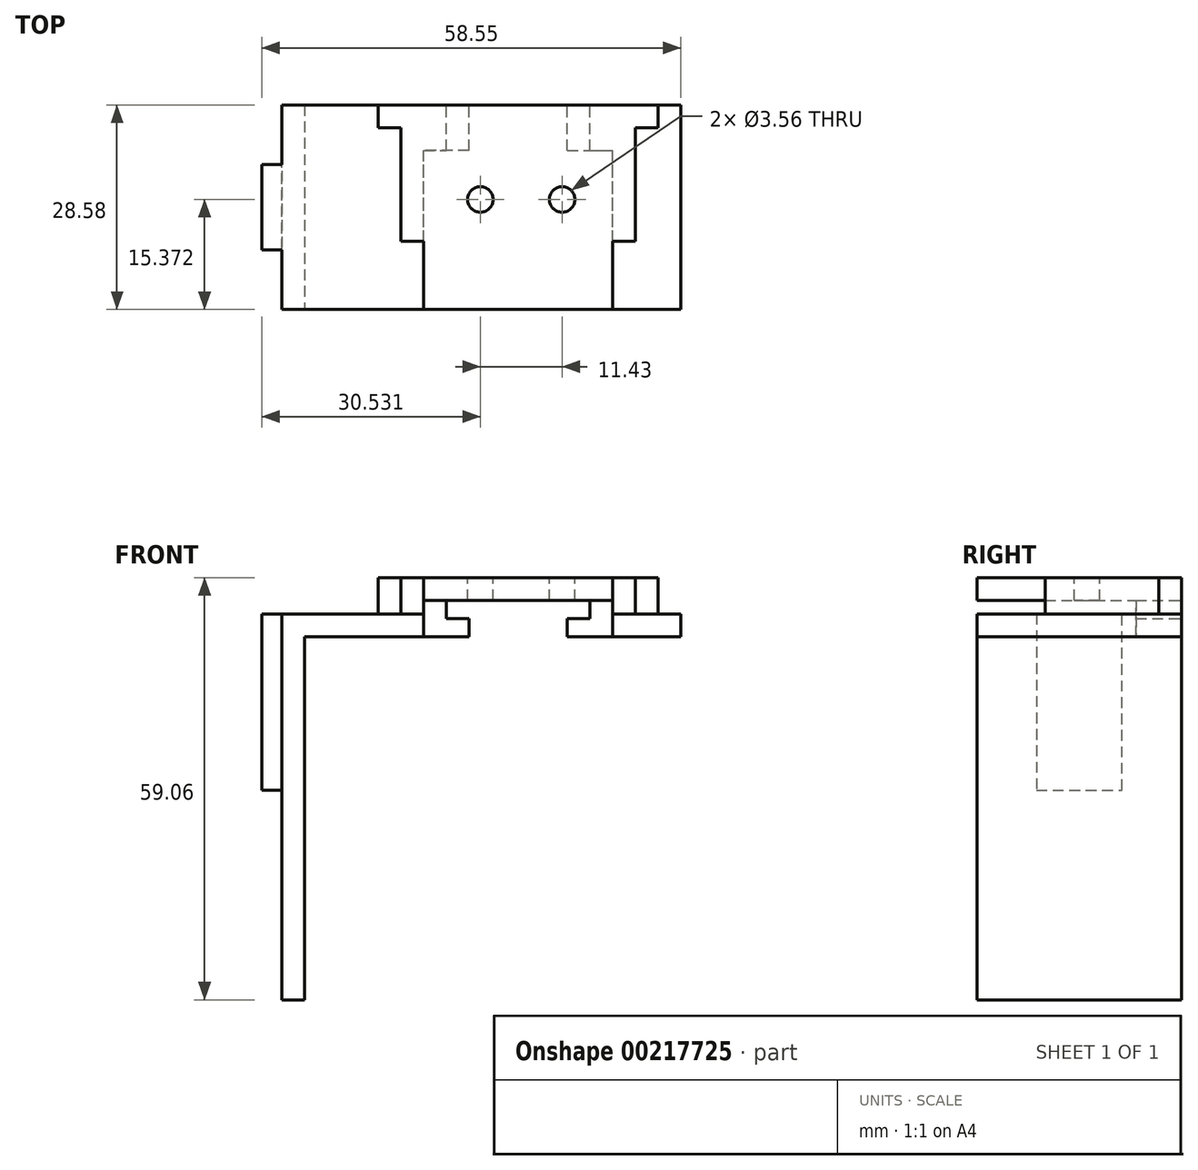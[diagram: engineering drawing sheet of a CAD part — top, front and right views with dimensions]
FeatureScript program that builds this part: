
annotation { "Feature Type Name" : "Feature", "Feature Type Description" : "" }
export const myFeature = defineFeature(function(context is Context, id is Id, definition is map)
    precondition{}
    {
        {
            var Q0;
            Q0=qCreatedBy(makeId("Front.planeOp"),FACE);
            var sketch = newSketch(context, id + "F0", { "sketchPlane" : qUnion([Q0])});
            skLineSegment(sketch, "E0", {"start": v(0, 0) * mm, "end": v(3.18, 0) * mm});
            skLineSegment(sketch, "E1", {"start": v(0, 0) * mm, "end": v(0, 2.54) * mm});
            skLineSegment(sketch, "E2", {"start": v(0, 2.54) * mm, "end": v(3.18, 2.54) * mm});
            skLineSegment(sketch, "E3", {"start": v(3.18, 0) * mm, "end": v(6.35, 0) * mm});
            skLineSegment(sketch, "E4", {"start": v(6.35, 0) * mm, "end": v(6.35, 5.08) * mm});
            skLineSegment(sketch, "E5.MirrorCS", {"start": v(-20.07, 0) * mm, "end": v(-20.07, 5.08) * mm});
            skLineSegment(sketch, "E6.MirrorCS", {"start": v(-16.9, 0) * mm, "end": v(-20.07, 0) * mm});
            skLineSegment(sketch, "E7.MirrorCS", {"start": v(-13.72, 0) * mm, "end": v(-13.72, 2.54) * mm});
            skLineSegment(sketch, "E8.MirrorCS", {"start": v(-13.72, 2.54) * mm, "end": v(-16.9, 2.54) * mm});
            skLineSegment(sketch, "E9.MirrorCS", {"start": v(-13.72, 0) * mm, "end": v(-16.9, 0) * mm});
            skLineSegment(sketch, "E10", {"start": v(-16.9, 2.54) * mm, "end": v(-16.9, 5.08) * mm});
            skLineSegment(sketch, "E11", {"start": v(-16.9, 5.08) * mm, "end": v(3.18, 5.08) * mm});
            skLineSegment(sketch, "E12", {"start": v(3.18, 5.08) * mm, "end": v(3.18, 2.54) * mm});
            skLineSegment(sketch, "E13", {"start": v(6.35, 5.08) * mm, "end": v(6.35, 8.26) * mm});
            skLineSegment(sketch, "E14", {"start": v(6.35, 8.26) * mm, "end": v(-20.07, 8.26) * mm});
            skLineSegment(sketch, "E15", {"start": v(-20.07, 8.26) * mm, "end": v(-20.07, 5.08) * mm});
            skSolve(sketch);
        }
        {
            var Q0;
            Q0 = qSketchRegion(id + "F0", true);
            extrude(context, id + "F1", {"entities" : qUnion([Q0]), "depth" : 6.35 * mm});
        }
        {
            var Q0;
            Q0=makeQuery(id+"F1.opExtrude","CAP_FACE",FACE,{"disambiguationData":[OSD([sQuery(id+"F0.wireOp",EDGE,"E0"),sQuery(id+"F0.wireOp",EDGE,"E1"),sQuery(id+"F0.wireOp",EDGE,"E2"),sQuery(id+"F0.wireOp",EDGE,"E3"),sQuery(id+"F0.wireOp",EDGE,"E4"),sQuery(id+"F0.wireOp",EDGE,"E5.MirrorCS"),sQuery(id+"F0.wireOp",EDGE,"E6.MirrorCS"),sQuery(id+"F0.wireOp",EDGE,"E7.MirrorCS"),sQuery(id+"F0.wireOp",EDGE,"E8.MirrorCS"),sQuery(id+"F0.wireOp",EDGE,"E9.MirrorCS"),sQuery(id+"F0.wireOp",EDGE,"E10"),sQuery(id+"F0.wireOp",EDGE,"E11"),sQuery(id+"F0.wireOp",EDGE,"E12"),sQuery(id+"F0.wireOp",EDGE,"E13"),sQuery(id+"F0.wireOp",EDGE,"E14"),sQuery(id+"F0.wireOp",EDGE,"E15")])],"isStart":false});
            var sketch = newSketch(context, id + "F2", { "sketchPlane" : qUnion([Q0])});
            skLineSegment(sketch, "E16.bottom", {"start": v(-20.07, 8.26) * mm, "end": v(6.35, 8.26) * mm});
            skLineSegment(sketch, "E16.top", {"start": v(-20.07, 5.08) * mm, "end": v(6.35, 5.08) * mm});
            skLineSegment(sketch, "E16.left", {"start": v(-20.07, 8.26) * mm, "end": v(-20.07, 5.08) * mm});
            skLineSegment(sketch, "E16.right", {"start": v(6.35, 8.26) * mm, "end": v(6.35, 5.08) * mm});
            skSolve(sketch);
        }
        {
            var Q0;
            Q0 = qSketchRegion(id + "F2", true);
            extrude(context, id + "F3", {"entities" : qUnion([Q0]), "operationType" : NewBodyOperationType.ADD, "depth" : 22.22 * mm});
        }
        {
            var Q0;
            Q0=makeQuery(id+"F3.boolean.opBoolean","MERGE",FACE,{"derivedFrom":[makeQuery(id+"F1.opExtrude","SWEPT_FACE",FACE,{"disambiguationData":[OSD([sQuery(id+"F0.wireOp",EDGE,"E14")])]}),makeQuery(id+"F3.opExtrude","SWEPT_FACE",FACE,{"disambiguationData":[OSD([sQuery(id+"F2.wireOp",EDGE,"E16.bottom")])]})]});
            var sketch = newSketch(context, id + "F4", { "sketchPlane" : qUnion([Q0])});
            skLineSegment(sketch, "E17.bottom", {"start": v(-20.07, 0) * mm, "end": v(-23.24, 0) * mm});
            skLineSegment(sketch, "E17.top", {"start": v(-20.07, -19.05) * mm, "end": v(-23.24, -19.05) * mm});
            skLineSegment(sketch, "E17.left", {"start": v(-20.07, 0) * mm, "end": v(-20.07, -19.05) * mm});
            skLineSegment(sketch, "E17.right", {"start": v(-23.24, 0) * mm, "end": v(-23.24, -19.05) * mm});
            skLineSegment(sketch, "E18.bottom", {"start": v(6.35, 0) * mm, "end": v(9.53, 0) * mm});
            skLineSegment(sketch, "E18.top", {"start": v(6.35, -19.05) * mm, "end": v(9.53, -19.05) * mm});
            skLineSegment(sketch, "E18.left", {"start": v(6.35, 0) * mm, "end": v(6.35, -19.05) * mm});
            skLineSegment(sketch, "E18.right", {"start": v(9.53, 0) * mm, "end": v(9.53, -19.05) * mm});
            skSolve(sketch);
        }
        {
            var Q0;
            Q0 = qSketchRegion(id + "F4", true);
            var Q1;
            Q1=makeQuery(id+"F1.opExtrude","SWEPT_FACE",FACE,{"disambiguationData":[OSD([sQuery(id+"F0.wireOp",EDGE,"E6.MirrorCS"),sQuery(id+"F0.wireOp",EDGE,"E9.MirrorCS")])]});
            extrude(context, id + "F5", {"entities" : qUnion([Q0]), "operationType" : NewBodyOperationType.ADD, "endBound" : BoundingType.UP_TO_SURFACE, "oppositeDirection" : true, "endBoundEntityFace" : qUnion([Q1]), "depth" : 9.52 * mm});
        }
        {
            var Q0;
            Q0=makeQuery(id+"F5.opExtrude","SWEPT_FACE",FACE,{"disambiguationData":[OSD([sQuery(id+"F4.wireOp",EDGE,"E17.top")])]});
            var sketch = newSketch(context, id + "F6", { "sketchPlane" : qUnion([Q0])});
            skLineSegment(sketch, "E19.bottom", {"start": v(-20.07, 0) * mm, "end": v(-23.24, 0) * mm});
            skLineSegment(sketch, "E19.top", {"start": v(-20.07, 3.18) * mm, "end": v(-23.24, 3.18) * mm});
            skLineSegment(sketch, "E19.left", {"start": v(-20.07, 0) * mm, "end": v(-20.07, 3.18) * mm});
            skLineSegment(sketch, "E19.right", {"start": v(-23.24, 0) * mm, "end": v(-23.24, 3.17) * mm});
            skSolve(sketch);
        }
        {
            var Q0;
            Q0 = qSketchRegion(id + "F6", true);
            var Q1;
            Q1=makeQuery(id+"F3.opExtrude","CAP_FACE",FACE,{"disambiguationData":[OSD([sQuery(id+"F2.wireOp",EDGE,"E16.bottom"),sQuery(id+"F2.wireOp",EDGE,"E16.top"),sQuery(id+"F2.wireOp",EDGE,"E16.left"),sQuery(id+"F2.wireOp",EDGE,"E16.right")])],"isStart":false});
            extrude(context, id + "F7", {"entities" : qUnion([Q0]), "operationType" : NewBodyOperationType.ADD, "endBound" : BoundingType.UP_TO_SURFACE, "endBoundEntityFace" : qUnion([Q1]), "depth" : 25.4 * mm});
        }
        {
            var Q0;
            Q0=makeQuery(id+"F5.opExtrude","SWEPT_FACE",FACE,{"disambiguationData":[OSD([sQuery(id+"F4.wireOp",EDGE,"E18.top")])]});
            var sketch = newSketch(context, id + "F8", { "sketchPlane" : qUnion([Q0])});
            skLineSegment(sketch, "E20.bottom", {"start": v(6.35, 0) * mm, "end": v(9.53, 0) * mm});
            skLineSegment(sketch, "E20.top", {"start": v(6.35, 3.18) * mm, "end": v(9.53, 3.18) * mm});
            skLineSegment(sketch, "E20.left", {"start": v(6.35, 0) * mm, "end": v(6.35, 3.18) * mm});
            skLineSegment(sketch, "E20.right", {"start": v(9.53, 0) * mm, "end": v(9.53, 3.18) * mm});
            skSolve(sketch);
        }
        {
            var Q0;
            Q0 = qSketchRegion(id + "F8", true);
            var Q1;
            Q1=makeQuery(id+"F3.opExtrude","CAP_FACE",FACE,{"disambiguationData":[OSD([sQuery(id+"F2.wireOp",EDGE,"E16.bottom"),sQuery(id+"F2.wireOp",EDGE,"E16.top"),sQuery(id+"F2.wireOp",EDGE,"E16.left"),sQuery(id+"F2.wireOp",EDGE,"E16.right")])],"isStart":false});
            extrude(context, id + "F9", {"entities" : qUnion([Q0]), "operationType" : NewBodyOperationType.ADD, "endBound" : BoundingType.UP_TO_SURFACE, "endBoundEntityFace" : qUnion([Q1]), "depth" : 25.4 * mm});
        }
        {
            var Q0;
            Q0=makeQuery(id+"F7.boolean.opBoolean","MERGE",FACE,{"derivedFrom":[makeQuery(id+"F5.opExtrude","SWEPT_FACE",FACE,{"disambiguationData":[OSD([sQuery(id+"F4.wireOp",EDGE,"E17.right")])]}),makeQuery(id+"F7.opExtrude","SWEPT_FACE",FACE,{"disambiguationData":[OSD([sQuery(id+"F6.wireOp",EDGE,"E19.right")])]})]});
            var sketch = newSketch(context, id + "F10", { "sketchPlane" : qUnion([Q0])});
            skLineSegment(sketch, "E21.bottom", {"start": v(28.57, 3.17) * mm, "end": v(0, 3.17) * mm});
            skLineSegment(sketch, "E21.top", {"start": v(28.57, 0) * mm, "end": v(0, 0) * mm});
            skLineSegment(sketch, "E21.left", {"start": v(28.57, 3.17) * mm, "end": v(28.57, 0) * mm});
            skLineSegment(sketch, "E21.right", {"start": v(0, 3.17) * mm, "end": v(0, 0) * mm});
            skSolve(sketch);
        }
        {
            var Q0;
            Q0 = qSketchRegion(id + "F10", true);
            extrude(context, id + "F11", {"entities" : qUnion([Q0]), "operationType" : NewBodyOperationType.ADD, "depth" : 13.46 * mm});
        }
        {
            var Q0;
            {var subQ0=sQuery(id+"F0.wireOp",EDGE,"E9.MirrorCS");var subQ1=sQuery(id+"F0.wireOp",EDGE,"E6.MirrorCS");Q0=makeQuery(id+"F11.boolean.opBoolean","MERGE",FACE,{"derivedFrom":[makeQuery(id+"F7.boolean.opBoolean","MERGE",FACE,{"derivedFrom":[makeQuery(id+"F5.boolean.opBoolean","MERGE",FACE,{"derivedFrom":[makeQuery(id+"F1.opExtrude","SWEPT_FACE",FACE,{"disambiguationData":[OSD([subQ1,subQ0])]}),makeQuery(id+"F5.opExtrude","CAP_FACE",FACE,{"disambiguationData":[OSD([subQ1,subQ0]),ownerDisambiguation([makeQuery(id+"F4.imprint","IMPRINT",EDGE,{"derivedFrom":sQuery(id+"F4.wireOp",EDGE,"E17.bottom")})])],"isStart":false})]}),makeQuery(id+"F7.opExtrude","SWEPT_FACE",FACE,{"disambiguationData":[OSD([sQuery(id+"F6.wireOp",EDGE,"E19.bottom")])]})]}),makeQuery(id+"F11.opExtrude","SWEPT_FACE",FACE,{"disambiguationData":[OSD([sQuery(id+"F10.wireOp",EDGE,"E21.top")])]})]});}
            var sketch = newSketch(context, id + "F12", { "sketchPlane" : qUnion([Q0])});
            skLineSegment(sketch, "E22.bottom", {"start": v(-36.7, 0) * mm, "end": v(-39.88, 0) * mm});
            skLineSegment(sketch, "E22.top", {"start": v(-36.7, 28.58) * mm, "end": v(-39.88, 28.58) * mm});
            skLineSegment(sketch, "E22.left", {"start": v(-36.7, 0) * mm, "end": v(-36.7, 28.58) * mm});
            skLineSegment(sketch, "E22.right", {"start": v(-39.88, 0) * mm, "end": v(-39.88, 28.58) * mm});
            skSolve(sketch);
        }
        {
            var Q0;
            Q0 = qSketchRegion(id + "F12", true);
            extrude(context, id + "F13", {"entities" : qUnion([Q0]), "operationType" : NewBodyOperationType.ADD, "depth" : 50.8 * mm, "hasSecondDirection" : true, "secondDirectionOppositeDirection" : true, "secondDirectionDepth" : 3.17 * mm});
        }
        {
            var Q0;
            Q0=makeQuery(id+"F13.opExtrude","SWEPT_FACE",FACE,{"disambiguationData":[OSD([sQuery(id+"F12.wireOp",EDGE,"E22.right")])]});
            var sketch = newSketch(context, id + "F14", { "sketchPlane" : qUnion([Q0])});
            skLineSegment(sketch, "E23", {"start": v(14.29, 3.18) * mm, "end": v(20.26, 3.18) * mm});
            skLineSegment(sketch, "E24", {"start": v(20.26, 3.18) * mm, "end": v(20.26, -21.46) * mm});
            skLineSegment(sketch, "E25", {"start": v(20.26, -21.46) * mm, "end": v(8.32, -21.46) * mm});
            skLineSegment(sketch, "E26", {"start": v(8.32, -21.46) * mm, "end": v(8.32, 3.17) * mm});
            skLineSegment(sketch, "E27", {"start": v(8.32, 3.18) * mm, "end": v(14.29, 3.18) * mm});
            skSolve(sketch);
        }
        {
            var Q0;
            Q0 = qSketchRegion(id + "F14", true);
            extrude(context, id + "F15", {"entities" : qUnion([Q0]), "operationType" : NewBodyOperationType.ADD, "depth" : 2.8 * mm});
        }
        {
            var Q0;
            Q0=makeQuery(id+"F5.boolean.opBoolean","MERGE",FACE,{"derivedFrom":[makeQuery(id+"F3.boolean.opBoolean","MERGE",FACE,{"derivedFrom":[makeQuery(id+"F1.opExtrude","SWEPT_FACE",FACE,{"disambiguationData":[OSD([sQuery(id+"F0.wireOp",EDGE,"E14")])]}),makeQuery(id+"F3.opExtrude","SWEPT_FACE",FACE,{"disambiguationData":[OSD([sQuery(id+"F2.wireOp",EDGE,"E16.bottom")])]})]}),makeQuery(id+"F5.opExtrude","CAP_FACE",FACE,{"disambiguationData":[OSD([sQuery(id+"F4.wireOp",EDGE,"E17.bottom"),sQuery(id+"F4.wireOp",EDGE,"E17.top"),sQuery(id+"F4.wireOp",EDGE,"E17.left"),sQuery(id+"F4.wireOp",EDGE,"E17.right")])],"isStart":true}),makeQuery(id+"F5.opExtrude","CAP_FACE",FACE,{"disambiguationData":[OSD([sQuery(id+"F4.wireOp",EDGE,"E18.bottom"),sQuery(id+"F4.wireOp",EDGE,"E18.top"),sQuery(id+"F4.wireOp",EDGE,"E18.left"),sQuery(id+"F4.wireOp",EDGE,"E18.right")])],"isStart":true})]});
            var sketch = newSketch(context, id + "F16", { "sketchPlane" : qUnion([Q0])});
            skLineSegment(sketch, "E28", {"start": v(-12.14, 0) * mm, "end": v(-12.14, -13.2) * mm});
            skCircle(sketch, "E29", {"center": v(-12.14, -13.2) * mm, "radius": 1.78 * mm});
            skLineSegment(sketch, "E30", {"start": v(-16.71, 0) * mm, "end": v(-12.14, 0) * mm});
            skLineSegment(sketch, "E31", {"start": v(-12.14, -13.2) * mm, "end": v(-0.7, -13.2) * mm});
            skCircle(sketch, "E32", {"center": v(-0.7, -13.2) * mm, "radius": 1.78 * mm});
            skSolve(sketch);
        }
        {
            var Q0;
            Q0 = qSketchRegion(id + "F16", true);
            extrude(context, id + "F17", {"entities" : qUnion([Q0]), "operationType" : NewBodyOperationType.REMOVE, "oppositeDirection" : true, "depth" : 25.4 * mm});
        }
        {
            var Q0;
            Q0=makeQuery(id+"F15.boolean.opBoolean","MERGE",FACE,{"derivedFrom":[makeQuery(id+"F13.boolean.opBoolean","MERGE",FACE,{"derivedFrom":[makeQuery(id+"F11.boolean.opBoolean","MERGE",FACE,{"derivedFrom":[makeQuery(id+"F7.opExtrude","SWEPT_FACE",FACE,{"disambiguationData":[OSD([sQuery(id+"F6.wireOp",EDGE,"E19.top")])]}),makeQuery(id+"F11.opExtrude","SWEPT_FACE",FACE,{"disambiguationData":[OSD([sQuery(id+"F10.wireOp",EDGE,"E21.bottom")])]})]}),makeQuery(id+"F13.opExtrude","CAP_FACE",FACE,{"disambiguationData":[OSD([sQuery(id+"F12.wireOp",EDGE,"E22.bottom"),sQuery(id+"F12.wireOp",EDGE,"E22.top"),sQuery(id+"F12.wireOp",EDGE,"E22.left"),sQuery(id+"F12.wireOp",EDGE,"E22.right")])],"isStart":true})]}),makeQuery(id+"F15.opExtrude","SWEPT_FACE",FACE,{"disambiguationData":[OSD([sQuery(id+"F14.wireOp",EDGE,"E23"),sQuery(id+"F14.wireOp",EDGE,"E27")])]})]});
            var sketch = newSketch(context, id + "F18", { "sketchPlane" : qUnion([Q0])});
            skLineSegment(sketch, "E33.bottom", {"start": v(-23.24, 0) * mm, "end": v(-26.42, 0) * mm});
            skLineSegment(sketch, "E33.top", {"start": v(-23.24, -3.17) * mm, "end": v(-26.42, -3.18) * mm});
            skLineSegment(sketch, "E33.left", {"start": v(-23.24, 0) * mm, "end": v(-23.24, -3.17) * mm});
            skLineSegment(sketch, "E33.right", {"start": v(-26.42, 0) * mm, "end": v(-26.42, -3.18) * mm});
            skSolve(sketch);
        }
        {
            var Q0;
            Q0 = qSketchRegion(id + "F18", true);
            var Q1;
            Q1=makeQuery(id+"F5.boolean.opBoolean","MERGE",FACE,{"derivedFrom":[makeQuery(id+"F3.boolean.opBoolean","MERGE",FACE,{"derivedFrom":[makeQuery(id+"F1.opExtrude","SWEPT_FACE",FACE,{"disambiguationData":[OSD([sQuery(id+"F0.wireOp",EDGE,"E14")])]}),makeQuery(id+"F3.opExtrude","SWEPT_FACE",FACE,{"disambiguationData":[OSD([sQuery(id+"F2.wireOp",EDGE,"E16.bottom")])]})]}),makeQuery(id+"F5.opExtrude","CAP_FACE",FACE,{"disambiguationData":[OSD([sQuery(id+"F4.wireOp",EDGE,"E17.bottom"),sQuery(id+"F4.wireOp",EDGE,"E17.top"),sQuery(id+"F4.wireOp",EDGE,"E17.left"),sQuery(id+"F4.wireOp",EDGE,"E17.right")])],"isStart":true}),makeQuery(id+"F5.opExtrude","CAP_FACE",FACE,{"disambiguationData":[OSD([sQuery(id+"F4.wireOp",EDGE,"E18.bottom"),sQuery(id+"F4.wireOp",EDGE,"E18.top"),sQuery(id+"F4.wireOp",EDGE,"E18.left"),sQuery(id+"F4.wireOp",EDGE,"E18.right")])],"isStart":true})]});
            extrude(context, id + "F19", {"entities" : qUnion([Q0]), "operationType" : NewBodyOperationType.ADD, "endBound" : BoundingType.UP_TO_SURFACE, "endBoundEntityFace" : qUnion([Q1]), "depth" : 25.4 * mm});
        }
        {
            var Q0;
            Q0=makeQuery(id+"F9.boolean.opBoolean","MERGE",FACE,{"derivedFrom":[makeQuery(id+"F5.opExtrude","SWEPT_FACE",FACE,{"disambiguationData":[OSD([sQuery(id+"F4.wireOp",EDGE,"E18.right")])]}),makeQuery(id+"F9.opExtrude","SWEPT_FACE",FACE,{"disambiguationData":[OSD([sQuery(id+"F8.wireOp",EDGE,"E20.right")])]})]});
            var sketch = newSketch(context, id + "F20", { "sketchPlane" : qUnion([Q0])});
            skLineSegment(sketch, "E34.bottom", {"start": v(-28.58, 3.18) * mm, "end": v(0, 3.18) * mm});
            skLineSegment(sketch, "E34.top", {"start": v(-28.58, 0) * mm, "end": v(0, 0) * mm});
            skLineSegment(sketch, "E34.left", {"start": v(-28.58, 3.18) * mm, "end": v(-28.58, 0) * mm});
            skLineSegment(sketch, "E34.right", {"start": v(0, 3.18) * mm, "end": v(0, 0) * mm});
            skSolve(sketch);
        }
        {
            var Q0;
            Q0 = qSketchRegion(id + "F20", true);
            extrude(context, id + "F21", {"entities" : qUnion([Q0]), "operationType" : NewBodyOperationType.ADD, "depth" : 6.35 * mm});
        }
        {
            var Q0;
            Q0=makeQuery(id+"F21.boolean.opBoolean","MERGE",FACE,{"derivedFrom":[makeQuery(id+"F9.opExtrude","SWEPT_FACE",FACE,{"disambiguationData":[OSD([sQuery(id+"F8.wireOp",EDGE,"E20.top")])]}),makeQuery(id+"F21.opExtrude","SWEPT_FACE",FACE,{"disambiguationData":[OSD([sQuery(id+"F20.wireOp",EDGE,"E34.bottom")])]})]});
            var sketch = newSketch(context, id + "F22", { "sketchPlane" : qUnion([Q0])});
            skLineSegment(sketch, "E35.bottom", {"start": v(9.53, 0) * mm, "end": v(12.7, 0) * mm});
            skLineSegment(sketch, "E35.top", {"start": v(9.53, -3.18) * mm, "end": v(12.7, -3.18) * mm});
            skLineSegment(sketch, "E35.left", {"start": v(9.53, 0) * mm, "end": v(9.53, -3.18) * mm});
            skLineSegment(sketch, "E35.right", {"start": v(12.7, 0) * mm, "end": v(12.7, -3.18) * mm});
            skSolve(sketch);
        }
        {
            var Q0;
            Q0 = qSketchRegion(id + "F22", true);
            var Q1;
            {var subQ0=sQuery(id+"F4.wireOp",EDGE,"E18.right");var subQ1=sQuery(id+"F4.wireOp",EDGE,"E18.left");var subQ2=sQuery(id+"F4.wireOp",EDGE,"E18.top");var subQ3=sQuery(id+"F4.wireOp",EDGE,"E18.bottom");var subQ4=sQuery(id+"F4.wireOp",EDGE,"E17.right");var subQ5=sQuery(id+"F4.wireOp",EDGE,"E17.left");var subQ6=sQuery(id+"F4.wireOp",EDGE,"E17.top");var subQ7=sQuery(id+"F4.wireOp",EDGE,"E17.bottom");var subQ8=sQuery(id+"F2.wireOp",EDGE,"E16.bottom");var subQ9=sQuery(id+"F0.wireOp",EDGE,"E14");Q1=makeQuery(id+"F19.boolean.opBoolean","MERGE",FACE,{"derivedFrom":[makeQuery(id+"F5.boolean.opBoolean","MERGE",FACE,{"derivedFrom":[makeQuery(id+"F3.boolean.opBoolean","MERGE",FACE,{"derivedFrom":[makeQuery(id+"F1.opExtrude","SWEPT_FACE",FACE,{"disambiguationData":[OSD([subQ9])]}),makeQuery(id+"F3.opExtrude","SWEPT_FACE",FACE,{"disambiguationData":[OSD([subQ8])]})]}),makeQuery(id+"F5.opExtrude","CAP_FACE",FACE,{"disambiguationData":[OSD([subQ7,subQ6,subQ5,subQ4])],"isStart":true}),makeQuery(id+"F5.opExtrude","CAP_FACE",FACE,{"disambiguationData":[OSD([subQ3,subQ2,subQ1,subQ0])],"isStart":true})]}),makeQuery(id+"F19.opExtrude","CAP_FACE",FACE,{"disambiguationData":[OSD([subQ9,subQ8,subQ7,subQ6,subQ5,subQ4,subQ3,subQ2,subQ1,subQ0])],"isStart":false})]});}
            extrude(context, id + "F23", {"entities" : qUnion([Q0]), "operationType" : NewBodyOperationType.ADD, "endBound" : BoundingType.UP_TO_SURFACE, "endBoundEntityFace" : qUnion([Q1]), "depth" : 25.4 * mm});
        }
    });
